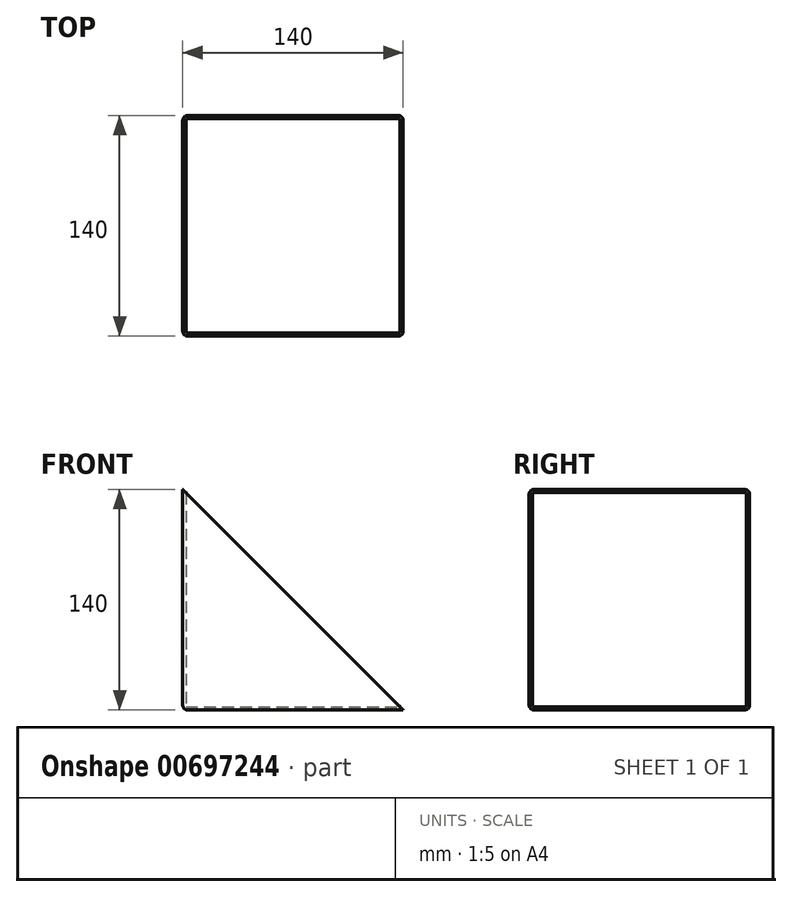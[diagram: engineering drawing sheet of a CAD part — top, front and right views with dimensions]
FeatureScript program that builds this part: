
annotation { "Feature Type Name" : "Feature", "Feature Type Description" : "" }
export const myFeature = defineFeature(function(context is Context, id is Id, definition is map)
    precondition{}
    {
        {
            var Q0;
            Q0=qCreatedBy(makeId("Front.planeOp"),FACE);
            var sketch = newSketch(context, id + "F0", { "sketchPlane" : qUnion([Q0])});
            skLineSegment(sketch, "E0", {"start": v(-140, 46.05) * mm, "end": v(-140, -93.95) * mm});
            skLineSegment(sketch, "E1", {"start": v(-140, -93.95) * mm, "end": v(0, -93.95) * mm});
            skLineSegment(sketch, "E2", {"start": v(0, -93.95) * mm, "end": v(-140, 46.05) * mm});
            skSolve(sketch);
        }
        {
            var Q0;
            Q0 = qSketchRegion(id + "F0", true);
            extrude(context, id + "F1", {"entities" : qUnion([Q0]), "depth" : 140 * mm, "offsetDistance" : 25 * mm});
        }
        {
            var Q0;
            Q0=makeQuery(id+"F1.opExtrude","SWEPT_FACE",FACE,{"disambiguationData":[OSD([sQuery(id+"F0.wireOp",EDGE,"E2")])]});
            shell(context, id + "F2", {"entities" : qUnion([Q0]), "thickness" : 2 * mm});
        }
        {
            var Q0;
            Q0=makeQuery(id+"F1.opExtrude","SWEPT_EDGE",EDGE,{"disambiguationData":[OSD([sQuery(id+"F0.wireOp",EDGE,"E0"),sQuery(id+"F0.wireOp",EDGE,"E1")])]});
            var Q1;
            Q1=makeQuery(id+"F1.opExtrude","CAP_EDGE",EDGE,{"disambiguationData":[OSD([sQuery(id+"F0.wireOp",EDGE,"E0")])],"isStart":true});
            var Q2;
            Q2=makeQuery(id+"F1.opExtrude","CAP_EDGE",EDGE,{"disambiguationData":[OSD([sQuery(id+"F0.wireOp",EDGE,"E1")])],"isStart":true});
            var Q3;
            Q3=makeQuery(id+"F1.opExtrude","CAP_EDGE",EDGE,{"disambiguationData":[OSD([sQuery(id+"F0.wireOp",EDGE,"E1")])],"isStart":false});
            var Q4;
            Q4=makeQuery(id+"F1.opExtrude","CAP_EDGE",EDGE,{"disambiguationData":[OSD([sQuery(id+"F0.wireOp",EDGE,"E0")])],"isStart":false});
            fillet(context, id + "F3", {"entities" : qUnion([Q0, Q1, Q2, Q3, Q4]), "radius" : 3 * mm, "tangentPropagation" : true, "allowEdgeOverflow" : false});
        }
    });
